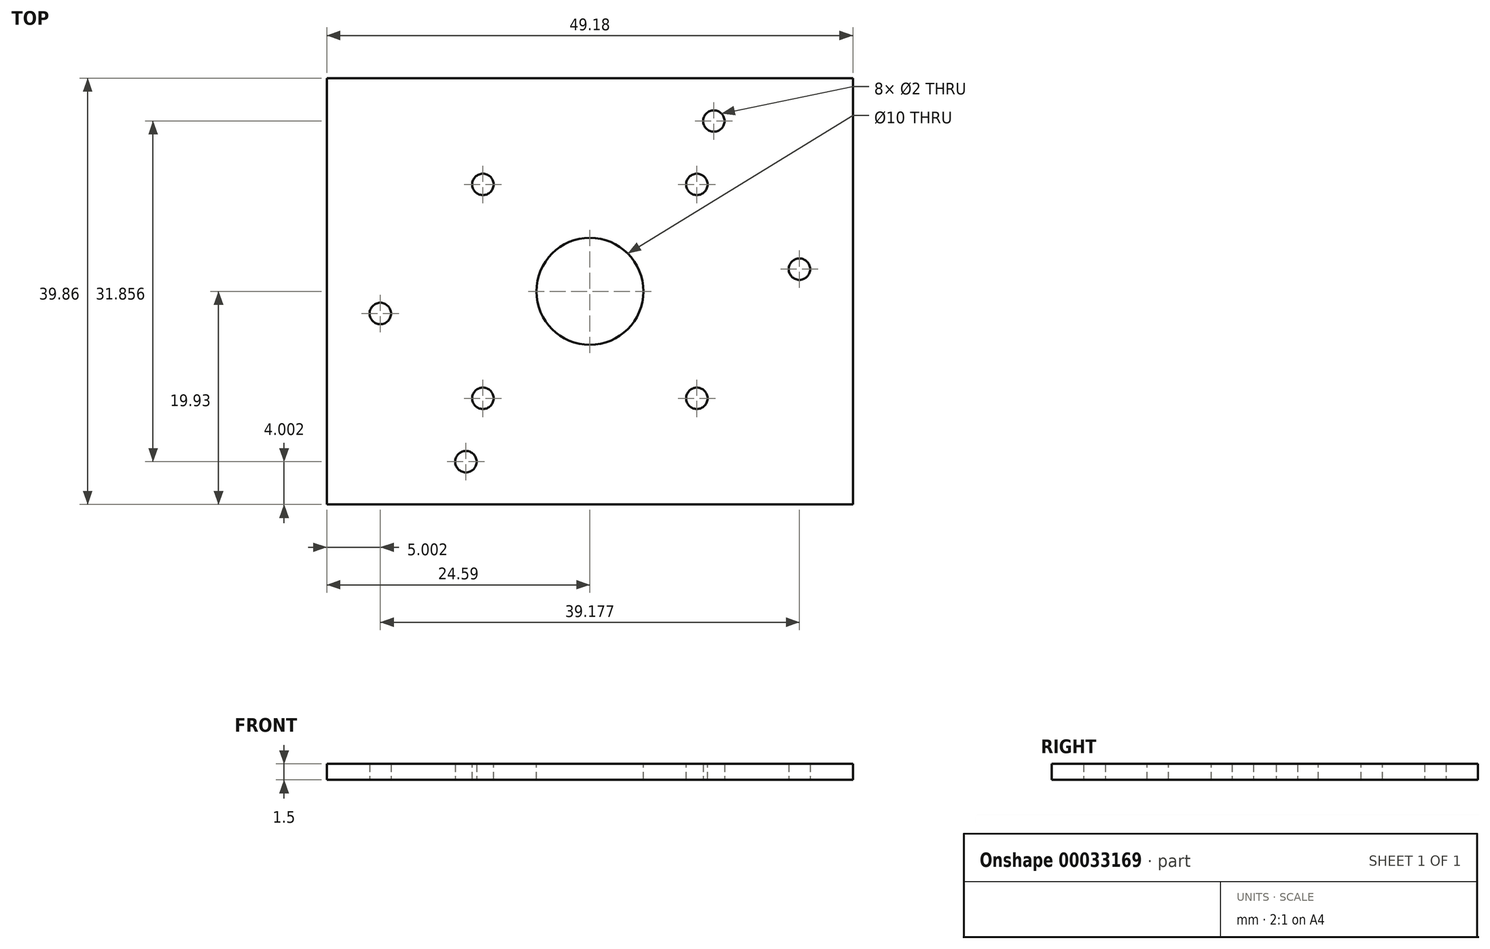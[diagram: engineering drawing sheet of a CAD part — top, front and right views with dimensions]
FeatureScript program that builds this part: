
annotation { "Feature Type Name" : "Feature", "Feature Type Description" : "" }
export const myFeature = defineFeature(function(context is Context, id is Id, definition is map)
    precondition{}
    {
        {
            var Q0;
            Q0=qCreatedBy(makeId("Top.planeOp"),FACE);
            var sketch = newSketch(context, id + "F0", { "sketchPlane" : qUnion([Q0])});
            skLineSegment(sketch, "E0.bottom", {"start": v(24.59, 19.93) * mm, "end": v(-24.59, 19.93) * mm});
            skLineSegment(sketch, "E0.top", {"start": v(24.59, -19.93) * mm, "end": v(-24.59, -19.93) * mm});
            skLineSegment(sketch, "E0.left", {"start": v(24.59, 19.93) * mm, "end": v(24.59, -19.93) * mm});
            skLineSegment(sketch, "E0.right", {"start": v(-24.59, 19.93) * mm, "end": v(-24.59, -19.93) * mm});
            skPoint(sketch, "E0.middle", {"position": v(0, 0) * mm});
            skCircle(sketch, "E1", {"center": v(11.59, 15.93) * mm, "radius": 1 * mm});
            skCircle(sketch, "E2", {"center": v(19.59, 2.07) * mm, "radius": 1 * mm});
            skLineSegment(sketch, "E3", {"start": v(11.59, 15.93) * mm, "end": v(19.59, 2.07) * mm, "construction": true});
            skLineSegment(sketch, "E4", {"start": v(11.59, 15.93) * mm, "end": v(-19.59, -2.07) * mm, "construction": true});
            skCircle(sketch, "E5", {"center": v(-19.59, -2.07) * mm, "radius": 1 * mm});
            skLineSegment(sketch, "E6", {"start": v(19.59, 2.07) * mm, "end": v(-11.59, -15.93) * mm, "construction": true});
            skLineSegment(sketch, "E7", {"start": v(-19.59, -2.07) * mm, "end": v(-11.59, -15.93) * mm, "construction": true});
            skCircle(sketch, "E8", {"center": v(-11.59, -15.93) * mm, "radius": 1 * mm});
            skPoint(sketch, "E9", {"position": v(-4, 6.93) * mm});
            skSolve(sketch);
        }
        {
            var Q0;
            Q0 = qSketchRegion(id + "F0", true);
            extrude(context, id + "F1", {"entities" : qUnion([Q0]), "depth" : 1.5 * mm});
        }
        {
            var Q0;
            Q0=makeQuery(id+"F1.opExtrude","CAP_FACE",FACE,{"disambiguationData":[OSD([sQuery(id+"F0.wireOp",EDGE,"E0.bottom"),sQuery(id+"F0.wireOp",EDGE,"E0.top"),sQuery(id+"F0.wireOp",EDGE,"E0.left"),sQuery(id+"F0.wireOp",EDGE,"E0.right"),sQuery(id+"F0.wireOp",EDGE,"E1"),sQuery(id+"F0.wireOp",EDGE,"E2"),sQuery(id+"F0.wireOp",EDGE,"E5"),sQuery(id+"F0.wireOp",EDGE,"E8")])],"isStart":false});
            var sketch = newSketch(context, id + "F2", { "sketchPlane" : qUnion([Q0])});
            skCircle(sketch, "E10", {"center": v(-10, 10) * mm, "radius": 1 * mm});
            skCircle(sketch, "E11.MirrorC", {"center": v(10, 10) * mm, "radius": 1 * mm});
            skCircle(sketch, "E12.MirrorC", {"center": v(-10, -10) * mm, "radius": 1 * mm});
            skCircle(sketch, "E13.MirrorC", {"center": v(10, -10) * mm, "radius": 1 * mm});
            skCircle(sketch, "E14", {"center": v(0, 0) * mm, "radius": 5 * mm});
            skSolve(sketch);
        }
        {
            var Q0;
            Q0 = qSketchRegion(id + "F2", true);
            extrude(context, id + "F3", {"entities" : qUnion([Q0]), "operationType" : NewBodyOperationType.REMOVE, "endBound" : BoundingType.UP_TO_NEXT, "oppositeDirection" : true, "depth" : 25 * mm});
        }
    });
